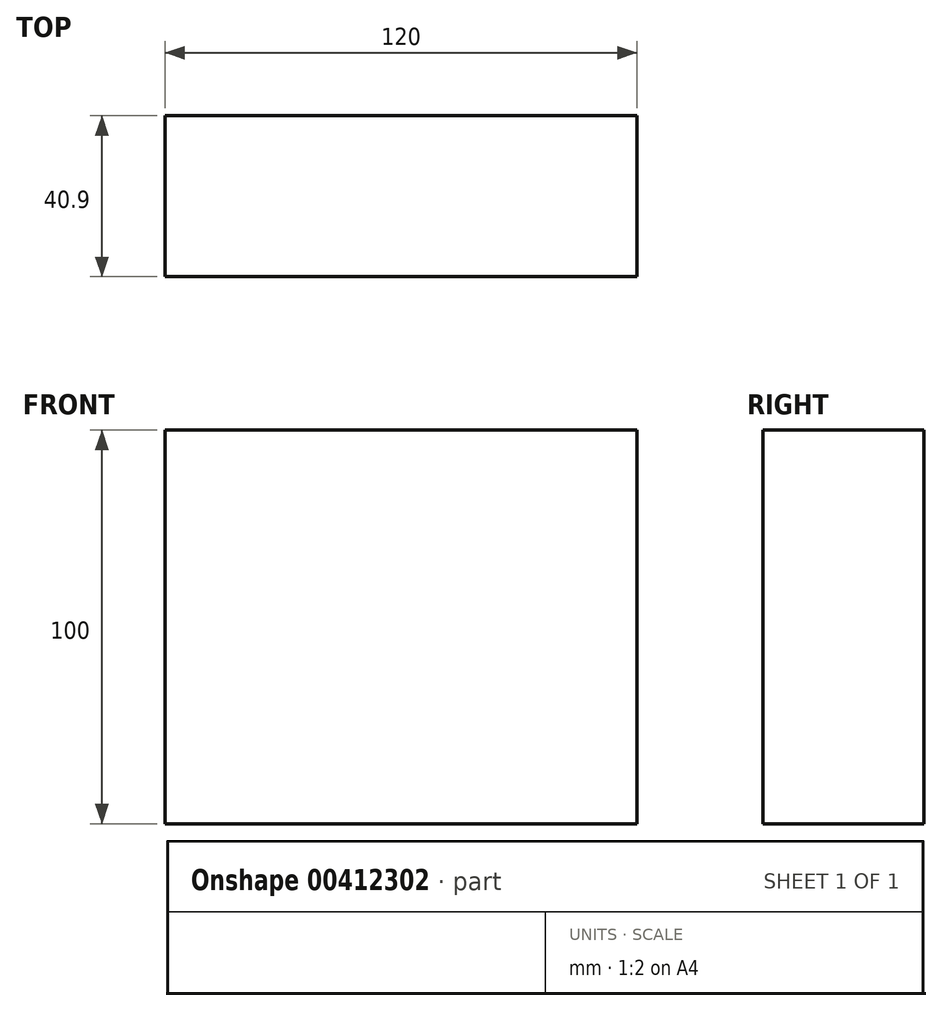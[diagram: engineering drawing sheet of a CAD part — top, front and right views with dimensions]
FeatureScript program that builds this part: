
annotation { "Feature Type Name" : "Feature", "Feature Type Description" : "" }
export const myFeature = defineFeature(function(context is Context, id is Id, definition is map)
    precondition{}
    {
        {
            var Q0;
            Q0=qCreatedBy(makeId("Front.planeOp"),FACE);
            var sketch = newSketch(context, id + "F0", { "sketchPlane" : qUnion([Q0])});
            skLineSegment(sketch, "E0.bottom", {"start": v(60, 50) * mm, "end": v(-60, 50) * mm});
            skLineSegment(sketch, "E0.top", {"start": v(60, -50) * mm, "end": v(-60, -50) * mm});
            skLineSegment(sketch, "E0.left", {"start": v(60, 50) * mm, "end": v(60, -50) * mm});
            skLineSegment(sketch, "E0.right", {"start": v(-60, 50) * mm, "end": v(-60, -50) * mm});
            skPoint(sketch, "E0.middle", {"position": v(0, 0) * mm});
            skSolve(sketch);
        }
        {
            var Q0;
            Q0 = qSketchRegion(id + "F0", true);
            extrude(context, id + "F1", {"entities" : qUnion([Q0]), "depth" : 40.9 * mm});
        }
    });
